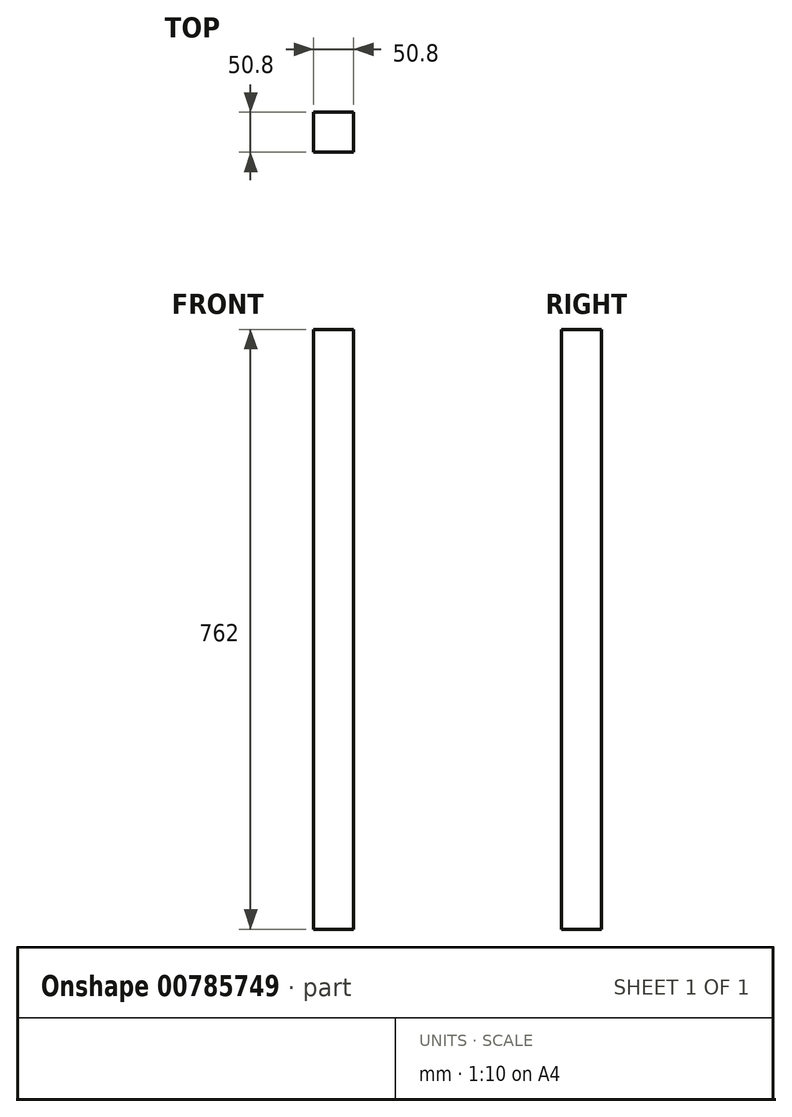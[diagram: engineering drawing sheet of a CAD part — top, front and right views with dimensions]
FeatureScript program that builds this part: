
annotation { "Feature Type Name" : "Feature", "Feature Type Description" : "" }
export const myFeature = defineFeature(function(context is Context, id is Id, definition is map)
    precondition{}
    {
        {
            var Q0;
            Q0=qCreatedBy(makeId("Right.planeOp"),FACE);
            var sketch = newSketch(context, id + "F0", { "sketchPlane" : qUnion([Q0])});
            skLineSegment(sketch, "E0.bottom", {"start": v(-65.97, 516.43) * mm, "end": v(-15.17, 516.43) * mm});
            skLineSegment(sketch, "E0.top", {"start": v(-65.97, -245.57) * mm, "end": v(-15.17, -245.57) * mm});
            skLineSegment(sketch, "E0.left", {"start": v(-65.97, 516.43) * mm, "end": v(-65.97, -245.57) * mm});
            skLineSegment(sketch, "E0.right", {"start": v(-15.17, 516.43) * mm, "end": v(-15.17, -245.57) * mm});
            skSolve(sketch);
        }
        {
            var Q0;
            Q0=makeQuery(id+"F0.imprint","IMPRINT",FACE,{"disambiguationData":[TD([[makeQuery(id+"F0.imprint","IMPRINT",EDGE,{"derivedFrom":sQuery(id+"F0.wireOp",EDGE,"E0.bottom")}),-1.0]])]});
            extrude(context, id + "F1", {"entities" : qUnion([Q0]), "depth" : 50.8 * mm, "offsetDistance" : 25.4 * mm});
        }
    });
